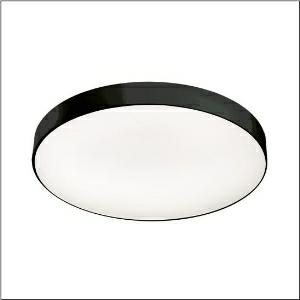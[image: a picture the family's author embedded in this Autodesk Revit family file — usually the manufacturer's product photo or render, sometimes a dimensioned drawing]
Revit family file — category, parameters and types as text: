
# Revit family: round_21_l_51mr38nd0421b
name_source: partatom
category: Lighting Fixtures
units: mm (PartAtom-declared; Revit-internal decimal feet)

## family parameters
Cut with Voids When Loaded = No
Host = Face
Light Source = No
Part Type = Normal
Room Calculation Point = No
Round Connector Dimension = Use Diameter
Shared = No

## types (1)
- Round 21 L (1 x LED, 12230 lm, 88.2 W, 4000K)
    Apparent Load = 88 VA
    CIE Flux Codes = 66 90 98 71 100
    Color Rendering = 80
    Color Temperature = 4000K
    Default Elevation = 1800 mm
    Description = Round 21 L, wall and ceiling luminaire, primary optical cover: micro prismatic cover, of PMMA, transparent, CAT 2 (L<= 3000cd/m²), light emission: direct/indirect distribution, primary light characteristic: symmetric, installation type: suspended mounting, surface-mounted, LED, rated luminous flux: 12.230lm, luminous efficacy: 139lm/W, light colour: 840, colour temperature: 4000K, control gear: DALI 2, with terminal, 5-pole, mains connection: 230V, AC, 50/60Hz, rated input power: 88W, housing, of aluminium, coated, black, diameter: 850mm, height: 62mm, protection rating (complete): IP40, insulation class (complete): insulation class I (protective earthing), certification: CE, impact resistance: IK04, permissible operating ambient temperature: -10..+35°C, packaging unit: 1 piece
    Height = 87 mm
    Lamp = 1 x LED
    Lamp Light Flux = 12230 lm
    Lamp Power = 88.2 W
    Lamp count = 1
    Length = 850 mm
    Luminous efficacy = 139 lm/W
    Manufacturer = Siteco
    ModVariant = No
    Model = 51MR38ND0421B
    Mounting Place = Ceiling
    Mounting Type = Surface mounted
    Number of Poles = 1
    OnlyDefault = Yes
    Power Factor = 1
    Product Name = Round 21 L
    Product group = wall and ceiling luminaire | ceiling mounted
    ProductGroupID = 304
    Protection Class = Protection class I
    Protection Degree = IP 40
    RLX_Detail_Level = 1
    RLX_Emergency_Light_Flux = 0 lm
    RLX_Emergency_Type = 0
    RLX_Emergency_Type_DB = No
    RlxData = <blob elided: 28757 chars, md5=03e97a8b>
    Socket = socket
    Standby Power = 0 W
    System Light Flux = 12230 lm
    System Power = 88 W
    Type Comments = Product without accessories
    Type Image = l_1258326.jpg
    URL = http://relux.com
    VarID = ---
    Voltage = 0 V
    Weight = 0.00 kg
    Width = 0 mm  [stored 0 ft]

note: [stored X ft] marks values corroborated as IEEE doubles in the binary element streams (Revit-internal decimal feet)

## geometry (parser evidence)
native form markers: Blend x4, Sweep x12
no freeform markers — native parametric forms only
